# Revit family: toilet-floor_mount-zurn-z5551-k
name_source: partatom
category: Plumbing Fixtures
units: mm (PartAtom-declared; Revit-internal decimal feet)

## family parameters
Cut with Voids When Loaded = No
Host = Face
Maintain Annotation Orientation = No
OmniClass Number = 23.45.05.21.11.11
OmniClass Title = Water Operated Water Closets
Part Type = Normal
Room Calculation Point = No
Round Connector Dimension = Use Radius
Shared = No

## types (1)
- Z5551-K (Elongated, Siphon Jet Toilet)
    ADA Compliance = Yes
    Assembly Code = D2010.60
    CW Connection = No
    CWFU = 0
    Default Elevation = 48 "
    Description = 1.6 gpf  ADA Height, Elongated, Elongated Jet Toilet
    Fixture Mounting Method = Floor Mounted
    Flush Rate (GPF) = 1.6
    HW Connection = No
    HWFU = 0
    Height of ( Bowl + Tank) = 30.125 "
    Height of Bowl = 16.719 "
    Height of Tank = 13.406 "
    Length of Tank = 8.5 "
    Main Material = Vitreous China - Zurn - White
    Manufacturer = Zurn Water, LLC
    Manufacturer Brand = Zurn
    Model = Z5551-K
    Modified Date = 01/09/2026
    Product Documentation Link = https://files.zurn.com
    Product Installation Sheet URL = https://files.zurn.com
    Product Page URL = https://www.zurn.com
    Product data URL = https://www.bimobject.com
    Repair Parts URL = https://files.zurn.com
    Sanitary Outlet  Pipe Radius (inch) = 1.5 "
    Shipping Weight (lbs) = 92
    URL = https://www.zurn.com
    Vent Connection = No
    WFU = 0
    Waste Connection = Yes
    Water Sense Compliance = No
    Width of ( Bowl + Tank) = 29.063 "
    Width of Bowl = 14.75 "
    Width of Tank = 18 "

## geometry (parser evidence)
native form markers: Sweep x8
no freeform markers — native parametric forms only
